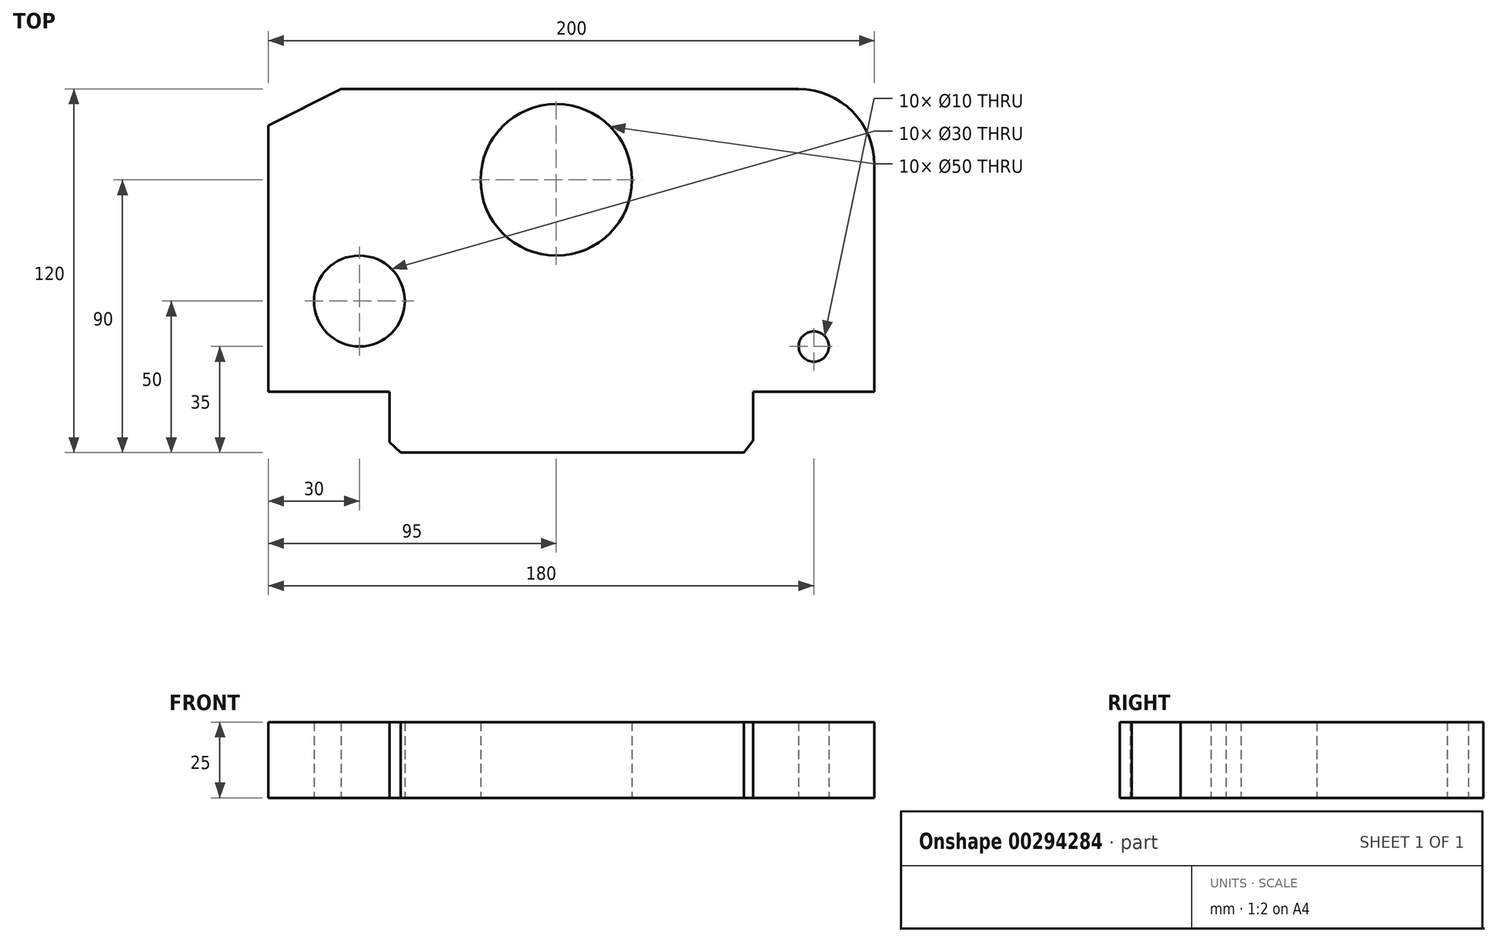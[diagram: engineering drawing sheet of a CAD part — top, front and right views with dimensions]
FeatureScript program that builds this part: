
annotation { "Feature Type Name" : "Feature", "Feature Type Description" : "" }
export const myFeature = defineFeature(function(context is Context, id is Id, definition is map)
    precondition{}
    {
        {
            var Q0;
            Q0=qCreatedBy(makeId("Top.planeOp"),FACE);
            var sketch = newSketch(context, id + "F0", { "sketchPlane" : qUnion([Q0])});
            skLineSegment(sketch, "E0", {"start": v(-112.42, 52.88) * mm, "end": v(-112.42, -35.12) * mm});
            skLineSegment(sketch, "E1", {"start": v(-112.42, -35.12) * mm, "end": v(-72.42, -35.12) * mm});
            skLineSegment(sketch, "E2", {"start": v(-72.42, -35.12) * mm, "end": v(-72.42, -51.75) * mm});
            skLineSegment(sketch, "E3", {"start": v(44.46, -55.12) * mm, "end": v(47.58, -51.21) * mm});
            skLineSegment(sketch, "E4", {"start": v(47.58, -51.21) * mm, "end": v(47.58, -35.12) * mm});
            skLineSegment(sketch, "E5", {"start": v(47.58, -35.12) * mm, "end": v(87.58, -35.12) * mm});
            skLineSegment(sketch, "E6", {"start": v(-112.42, 52.88) * mm, "end": v(-88.42, 64.88) * mm});
            skLineSegment(sketch, "E7", {"start": v(-88.42, 64.88) * mm, "end": v(62.58, 64.88) * mm});
            skLineSegment(sketch, "E8", {"start": v(87.58, -35.12) * mm, "end": v(87.58, 39.88) * mm});
            skPoint(sketch, "E9.start.orphan", {"position": v(-37.5, -55.12) * mm});
            skLineSegment(sketch, "E10", {"start": v(-72.42, -51.75) * mm, "end": v(-68.73, -55.12) * mm});
            skLineSegment(sketch, "E11", {"start": v(44.46, -55.12) * mm, "end": v(-68.73, -55.12) * mm});
            skPoint(sketch, "E12.visualSharp", {"position": v(87.58, 64.88) * mm});
            skArc(sketch, "E12.filletArc", {"start": v(87.58, 39.88) * mm, "mid": v(80.26, 57.56) * mm, "end": v(62.58, 64.88) * mm});
            skCircle(sketch, "E13", {"center": v(67.58, -20.12) * mm, "radius": 5 * mm});
            skCircle(sketch, "E14", {"center": v(-82.42, -5.12) * mm, "radius": 15 * mm});
            skCircle(sketch, "E15", {"center": v(-17.42, 34.88) * mm, "radius": 25 * mm});
            skSolve(sketch);
        }
        {
            var Q0;
            Q0 = qSketchRegion(id + "F0", true);
            extrude(context, id + "F1", {"entities" : qUnion([Q0]), "depth" : 25 * mm});
        }
    });
